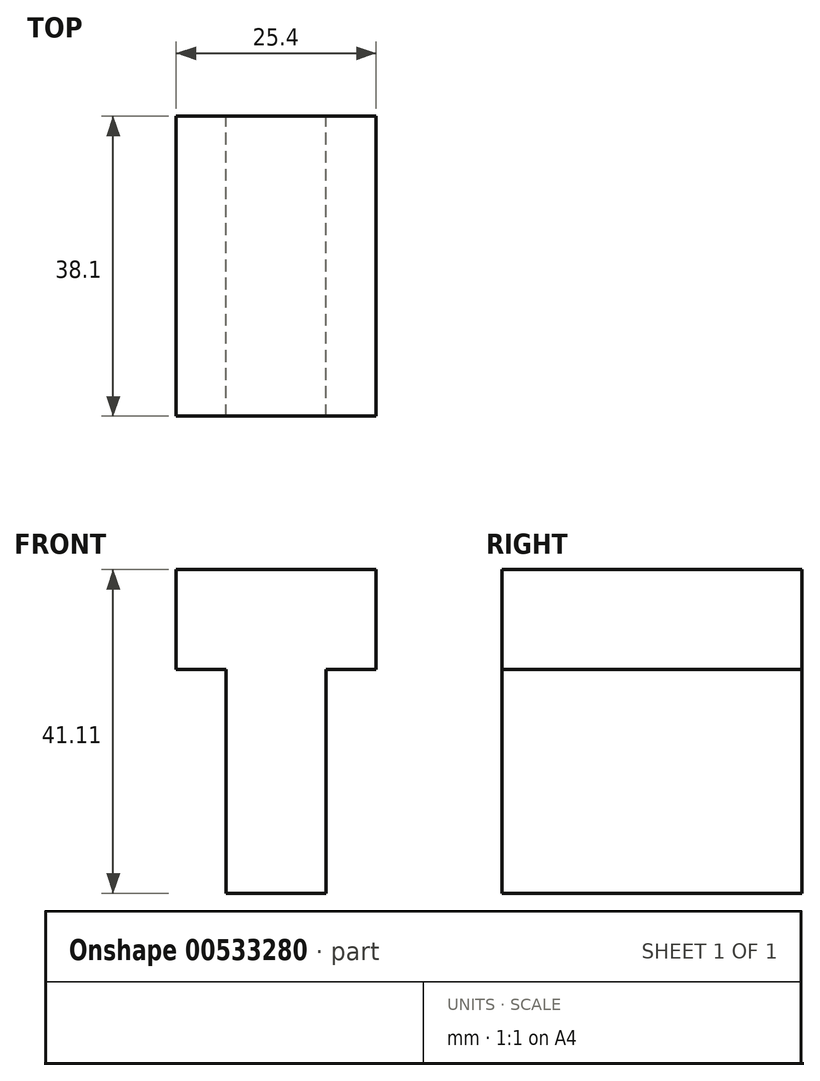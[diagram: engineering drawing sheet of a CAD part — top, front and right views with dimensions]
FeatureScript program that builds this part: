
annotation { "Feature Type Name" : "Feature", "Feature Type Description" : "" }
export const myFeature = defineFeature(function(context is Context, id is Id, definition is map)
    precondition{}
    {
        {
            var Q0;
            Q0=qCreatedBy(makeId("Front.planeOp"),FACE);
            var sketch = newSketch(context, id + "F0", { "sketchPlane" : qUnion([Q0])});
            skLineSegment(sketch, "E0", {"start": v(-52.38, 51.01) * mm, "end": v(-26.98, 51.01) * mm});
            skLineSegment(sketch, "E1", {"start": v(-52.38, 51.01) * mm, "end": v(-52.38, 38.31) * mm});
            skLineSegment(sketch, "E2", {"start": v(-26.98, 51.01) * mm, "end": v(-26.98, 38.31) * mm});
            skLineSegment(sketch, "E3", {"start": v(-52.38, 38.31) * mm, "end": v(-46.03, 38.31) * mm});
            skLineSegment(sketch, "E4", {"start": v(-26.98, 38.31) * mm, "end": v(-33.33, 38.31) * mm});
            skLineSegment(sketch, "E5", {"start": v(-46.03, 38.31) * mm, "end": v(-46.03, 9.9) * mm});
            skLineSegment(sketch, "E6", {"start": v(-46.03, 9.9) * mm, "end": v(-33.33, 9.9) * mm});
            skLineSegment(sketch, "E7", {"start": v(-33.33, 9.9) * mm, "end": v(-33.33, 38.31) * mm});
            skSolve(sketch);
        }
        {
            var Q0;
            Q0=makeQuery(id+"F0.imprint","IMPRINT",FACE,{"disambiguationData":[TD([[makeQuery(id+"F0.imprint","IMPRINT",EDGE,{"derivedFrom":sQuery(id+"F0.wireOp",EDGE,"E0")}),-1.0]])]});
            extrude(context, id + "F1", {"entities" : qUnion([Q0]), "depth" : 38.1 * mm, "offsetDistance" : 25.4 * mm});
        }
    });
